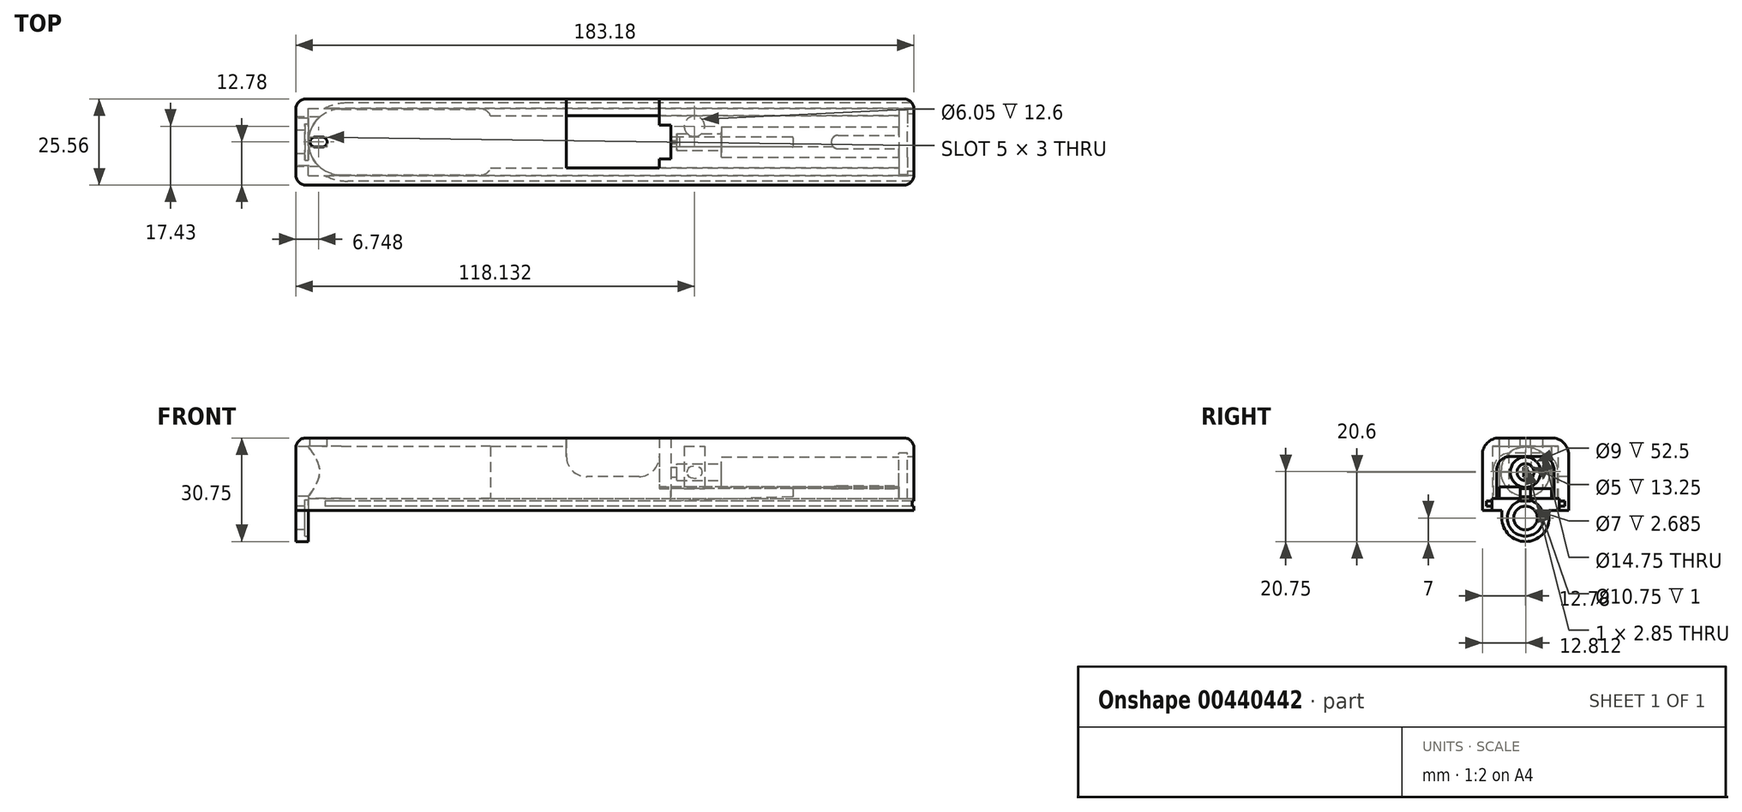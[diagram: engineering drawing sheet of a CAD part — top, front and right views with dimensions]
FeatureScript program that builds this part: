
annotation { "Feature Type Name" : "Feature", "Feature Type Description" : "" }
export const myFeature = defineFeature(function(context is Context, id is Id, definition is map)
    precondition{}
    {
        {
            var Q0;
            Q0=qCreatedBy(makeId("Top.planeOp"),FACE);
            var sketch = newSketch(context, id + "F0", { "sketchPlane" : qUnion([Q0])});
            skLineSegment(sketch, "E0.bottom", {"start": v(91.6, 12.78) * mm, "end": v(-91.6, 12.78) * mm});
            skLineSegment(sketch, "E0.top", {"start": v(91.6, -12.78) * mm, "end": v(-91.6, -12.78) * mm});
            skLineSegment(sketch, "E0.left", {"start": v(91.6, 12.78) * mm, "end": v(91.6, -12.78) * mm});
            skLineSegment(sketch, "E0.right", {"start": v(-91.6, 12.78) * mm, "end": v(-91.6, -12.78) * mm});
            skPoint(sketch, "E0.middle", {"position": v(0, 0) * mm});
            skSolve(sketch);
        }
        {
            var Q0;
            Q0 = qSketchRegion(id + "F0", true);
            extrude(context, id + "F1", {"entities" : qUnion([Q0]), "depth" : 21.5 * mm});
        }
        {
            var Q0;
            Q0=makeQuery(id+"F1.opExtrude","CAP_EDGE",EDGE,{"disambiguationData":[OSD([sQuery(id+"F0.wireOp",EDGE,"E0.top")])],"isStart":false});
            var Q1;
            Q1=makeQuery(id+"F1.opExtrude","CAP_EDGE",EDGE,{"disambiguationData":[OSD([sQuery(id+"F0.wireOp",EDGE,"E0.bottom")])],"isStart":false});
            fillet(context, id + "F2", {"entities" : qUnion([Q0, Q1]), "radius" : 5 * mm, "allowEdgeOverflow" : false});
        }
        {
            var Q0;
            Q0=makeQuery(id+"F1.opExtrude","SWEPT_EDGE",EDGE,{"disambiguationData":[OSD([sQuery(id+"F0.wireOp",EDGE,"E0.top"),sQuery(id+"F0.wireOp",EDGE,"E0.right")])]});
            var Q1;
            Q1=makeQuery(id+"F2.opFillet","BLEND_EDGE",EDGE,{"blendedFrom":[makeQuery(id+"F1.opExtrude","CAP_EDGE",EDGE,{"disambiguationData":[OSD([sQuery(id+"F0.wireOp",EDGE,"E0.top")])],"isStart":false}),makeQuery(id+"F1.opExtrude","SWEPT_FACE",FACE,{"disambiguationData":[OSD([sQuery(id+"F0.wireOp",EDGE,"E0.right")])]})],"blendedInto":[makeQuery(id+"F1.opExtrude","SWEPT_FACE",FACE,{"disambiguationData":[OSD([sQuery(id+"F0.wireOp",EDGE,"E0.right")])]})]});
            var Q2;
            Q2=makeQuery(id+"F1.opExtrude","CAP_EDGE",EDGE,{"disambiguationData":[OSD([sQuery(id+"F0.wireOp",EDGE,"E0.right")])],"isStart":false});
            var Q3;
            Q3=makeQuery(id+"F2.opFillet","BLEND_EDGE",EDGE,{"blendedFrom":[makeQuery(id+"F1.opExtrude","CAP_EDGE",EDGE,{"disambiguationData":[OSD([sQuery(id+"F0.wireOp",EDGE,"E0.bottom")])],"isStart":false}),makeQuery(id+"F1.opExtrude","SWEPT_FACE",FACE,{"disambiguationData":[OSD([sQuery(id+"F0.wireOp",EDGE,"E0.right")])]})],"blendedInto":[makeQuery(id+"F1.opExtrude","SWEPT_FACE",FACE,{"disambiguationData":[OSD([sQuery(id+"F0.wireOp",EDGE,"E0.right")])]})]});
            var Q4;
            Q4=makeQuery(id+"F1.opExtrude","SWEPT_EDGE",EDGE,{"disambiguationData":[OSD([sQuery(id+"F0.wireOp",EDGE,"E0.bottom"),sQuery(id+"F0.wireOp",EDGE,"E0.right")])]});
            var Q5;
            Q5=makeQuery(id+"F1.opExtrude","SWEPT_EDGE",EDGE,{"disambiguationData":[OSD([sQuery(id+"F0.wireOp",EDGE,"E0.top"),sQuery(id+"F0.wireOp",EDGE,"E0.left")])]});
            var Q6;
            Q6=makeQuery(id+"F2.opFillet","BLEND_EDGE",EDGE,{"blendedFrom":[makeQuery(id+"F1.opExtrude","CAP_EDGE",EDGE,{"disambiguationData":[OSD([sQuery(id+"F0.wireOp",EDGE,"E0.top")])],"isStart":false}),makeQuery(id+"F1.opExtrude","SWEPT_FACE",FACE,{"disambiguationData":[OSD([sQuery(id+"F0.wireOp",EDGE,"E0.left")])]})],"blendedInto":[makeQuery(id+"F1.opExtrude","SWEPT_FACE",FACE,{"disambiguationData":[OSD([sQuery(id+"F0.wireOp",EDGE,"E0.left")])]})]});
            var Q7;
            Q7=makeQuery(id+"F1.opExtrude","CAP_EDGE",EDGE,{"disambiguationData":[OSD([sQuery(id+"F0.wireOp",EDGE,"E0.left")])],"isStart":false});
            var Q8;
            Q8=makeQuery(id+"F2.opFillet","BLEND_EDGE",EDGE,{"blendedFrom":[makeQuery(id+"F1.opExtrude","CAP_EDGE",EDGE,{"disambiguationData":[OSD([sQuery(id+"F0.wireOp",EDGE,"E0.bottom")])],"isStart":false}),makeQuery(id+"F1.opExtrude","SWEPT_FACE",FACE,{"disambiguationData":[OSD([sQuery(id+"F0.wireOp",EDGE,"E0.left")])]})],"blendedInto":[makeQuery(id+"F1.opExtrude","SWEPT_FACE",FACE,{"disambiguationData":[OSD([sQuery(id+"F0.wireOp",EDGE,"E0.left")])]})]});
            var Q9;
            Q9=makeQuery(id+"F1.opExtrude","SWEPT_EDGE",EDGE,{"disambiguationData":[OSD([sQuery(id+"F0.wireOp",EDGE,"E0.bottom"),sQuery(id+"F0.wireOp",EDGE,"E0.left")])]});
            fillet(context, id + "F3", {"entities" : qUnion([Q0, Q1, Q2, Q3, Q4, Q5, Q6, Q7, Q8, Q9]), "radius" : 3 * mm, "tangentPropagation" : true, "allowEdgeOverflow" : false});
        }
        {
            var Q0;
            Q0=makeQuery(id+"F1.opExtrude","CAP_FACE",FACE,{"disambiguationData":[OSD([sQuery(id+"F0.wireOp",EDGE,"E0.bottom"),sQuery(id+"F0.wireOp",EDGE,"E0.top"),sQuery(id+"F0.wireOp",EDGE,"E0.left"),sQuery(id+"F0.wireOp",EDGE,"E0.right")])],"isStart":true});
            var sketch = newSketch(context, id + "F4", { "sketchPlane" : qUnion([Q0])});
            skLineSegment(sketch, "E1.bottom", {"start": v(-87.9, 10) * mm, "end": v(91.6, 10) * mm});
            skLineSegment(sketch, "E1.top", {"start": v(-87.9, -10) * mm, "end": v(91.6, -10) * mm});
            skLineSegment(sketch, "E1.left", {"start": v(-87.9, 10) * mm, "end": v(-87.9, -10) * mm});
            skLineSegment(sketch, "E1.right", {"start": v(91.6, 10) * mm, "end": v(91.6, -10) * mm});
            skPoint(sketch, "E1.middle", {"position": v(1.84, 0) * mm});
            skSolve(sketch);
        }
        {
            var Q0;
            Q0 = qSketchRegion(id + "F4", true);
            extrude(context, id + "F5", {"entities" : qUnion([Q0]), "operationType" : NewBodyOperationType.REMOVE, "oppositeDirection" : true, "depth" : 3.5 * mm});
        }
        {
            var Q0;
            Q0=makeQuery(id+"F5.boolean.opBoolean","COPY",FACE,{"derivedFrom":makeQuery(id+"F5.opExtrude","CAP_FACE",FACE,{"disambiguationData":[OSD([sQuery(id+"F4.wireOp",EDGE,"E1.bottom"),sQuery(id+"F4.wireOp",EDGE,"E1.top"),sQuery(id+"F4.wireOp",EDGE,"E1.left"),sQuery(id+"F4.wireOp",EDGE,"E1.right")])],"isStart":false})});
            var sketch = newSketch(context, id + "F6", { "sketchPlane" : qUnion([Q0])});
            skLineSegment(sketch, "E2.bottom", {"start": v(-87.9, -9.75) * mm, "end": v(-33.9, -9.75) * mm});
            skLineSegment(sketch, "E2.top", {"start": v(-87.9, 9.75) * mm, "end": v(-33.9, 9.75) * mm});
            skLineSegment(sketch, "E2.left", {"start": v(-87.9, -9.75) * mm, "end": v(-87.9, 9.75) * mm});
            skLineSegment(sketch, "E2.right", {"start": v(-33.9, -9.75) * mm, "end": v(-33.9, 9.75) * mm});
            skPoint(sketch, "E2.middle", {"position": v(-60.9, 0) * mm});
            skSolve(sketch);
        }
        {
            var Q0;
            Q0 = qSketchRegion(id + "F6", true);
            extrude(context, id + "F7", {"entities" : qUnion([Q0]), "operationType" : NewBodyOperationType.REMOVE, "oppositeDirection" : true, "depth" : 15.5 * mm});
        }
        {
            var Q0;
            Q0=makeQuery(id+"F5.boolean.opBoolean","COPY",FACE,{"derivedFrom":makeQuery(id+"F5.opExtrude","CAP_FACE",FACE,{"disambiguationData":[OSD([sQuery(id+"F4.wireOp",EDGE,"E1.bottom"),sQuery(id+"F4.wireOp",EDGE,"E1.top"),sQuery(id+"F4.wireOp",EDGE,"E1.left"),sQuery(id+"F4.wireOp",EDGE,"E1.right")])],"isStart":false})});
            var sketch = newSketch(context, id + "F8", { "sketchPlane" : qUnion([Q0])});
            skLineSegment(sketch, "E3.bottom", {"start": v(-33.9, -7.75) * mm, "end": v(16.1, -7.75) * mm});
            skLineSegment(sketch, "E3.top", {"start": v(-33.9, 7.75) * mm, "end": v(16.1, 7.75) * mm});
            skLineSegment(sketch, "E3.left", {"start": v(-33.9, -7.75) * mm, "end": v(-33.9, 7.75) * mm});
            skLineSegment(sketch, "E3.right", {"start": v(16.1, -7.75) * mm, "end": v(16.1, 7.75) * mm});
            skPoint(sketch, "E3.middle", {"position": v(-8.9, 0) * mm});
            skSolve(sketch);
        }
        {
            var Q0;
            Q0 = qSketchRegion(id + "F8", true);
            extrude(context, id + "F9", {"entities" : qUnion([Q0]), "operationType" : NewBodyOperationType.REMOVE, "oppositeDirection" : true, "depth" : 15.5 * mm});
        }
        {
            var Q0;
            Q0=makeQuery(id+"F5.boolean.opBoolean","COPY",FACE,{"derivedFrom":makeQuery(id+"F5.opExtrude","CAP_FACE",FACE,{"disambiguationData":[OSD([sQuery(id+"F4.wireOp",EDGE,"E1.bottom"),sQuery(id+"F4.wireOp",EDGE,"E1.top"),sQuery(id+"F4.wireOp",EDGE,"E1.left"),sQuery(id+"F4.wireOp",EDGE,"E1.right")])],"isStart":false})});
            var sketch = newSketch(context, id + "F10", { "sketchPlane" : qUnion([Q0])});
            skLineSegment(sketch, "E4.bottom", {"start": v(19.6, -5) * mm, "end": v(16.1, -5) * mm});
            skLineSegment(sketch, "E4.top", {"start": v(19.6, 5) * mm, "end": v(16.1, 5) * mm});
            skLineSegment(sketch, "E4.left", {"start": v(19.6, -5) * mm, "end": v(19.6, 5) * mm});
            skLineSegment(sketch, "E4.right", {"start": v(16.1, -5) * mm, "end": v(16.1, 5) * mm});
            skSolve(sketch);
        }
        {
            var Q0;
            Q0 = qSketchRegion(id + "F10", true);
            extrude(context, id + "F11", {"entities" : qUnion([Q0]), "operationType" : NewBodyOperationType.REMOVE, "endBound" : BoundingType.THROUGH_ALL, "oppositeDirection" : true, "depth" : 25.4 * mm});
        }
        {
            var Q0;
            Q0=makeQuery(id+"F1.opExtrude","CAP_FACE",FACE,{"disambiguationData":[OSD([sQuery(id+"F0.wireOp",EDGE,"E0.bottom"),sQuery(id+"F0.wireOp",EDGE,"E0.top"),sQuery(id+"F0.wireOp",EDGE,"E0.left"),sQuery(id+"F0.wireOp",EDGE,"E0.right")])],"isStart":false});
            var sketch = newSketch(context, id + "F12", { "sketchPlane" : qUnion([Q0])});
            skLineSegment(sketch, "E5.bottom", {"start": v(-11.4, 7.75) * mm, "end": v(16.1, 7.75) * mm});
            skLineSegment(sketch, "E5.top", {"start": v(-11.4, -7.75) * mm, "end": v(16.1, -7.75) * mm});
            skLineSegment(sketch, "E5.left", {"start": v(-11.4, 7.75) * mm, "end": v(-11.4, -7.75) * mm});
            skLineSegment(sketch, "E5.right", {"start": v(16.1, 7.75) * mm, "end": v(16.1, -7.75) * mm});
            skPoint(sketch, "E5.middle", {"position": v(2.34, 0) * mm});
            skSolve(sketch);
        }
        {
            var Q0;
            {var subQ3=sQuery(id+"F12.wireOp",EDGE,"E5.bottom");Q0=makeQuery(id+"F12.imprint","IMPRINT",FACE,{"disambiguationData":[TD([[makeQuery(id+"F12.imprint","IMPRINT",EDGE,{"derivedFrom":subQ3}),-1.0]])]});}
            extrude(context, id + "F13", {"entities" : qUnion([Q0]), "operationType" : NewBodyOperationType.REMOVE, "oppositeDirection" : true, "depth" : 25.4 * mm});
        }
        {
            var Q0;
            Q0=makeQuery(id+"F13.boolean.opBoolean","MERGE",FACE,{"derivedFrom":[makeQuery(id+"F9.boolean.opBoolean","COPY",FACE,{"derivedFrom":makeQuery(id+"F9.opExtrude","SWEPT_FACE",FACE,{"disambiguationData":[OSD([sQuery(id+"F8.wireOp",EDGE,"E3.top")])]})}),makeQuery(id+"F13.opExtrude","SWEPT_FACE",FACE,{"disambiguationData":[OSD([sQuery(id+"F12.wireOp",EDGE,"E5.top")])]})]});
            var sketch = newSketch(context, id + "F14", { "sketchPlane" : qUnion([Q0])});
            skLineSegment(sketch, "E6.bottom", {"start": v(11.4, 21.5) * mm, "end": v(-16.1, 21.5) * mm});
            skLineSegment(sketch, "E6.top", {"start": v(5.4, 10) * mm, "end": v(-10.1, 10) * mm});
            skLineSegment(sketch, "E6.left", {"start": v(11.4, 21.5) * mm, "end": v(11.4, 16) * mm});
            skLineSegment(sketch, "E6.right", {"start": v(-16.1, 21.5) * mm, "end": v(-16.1, 16) * mm});
            skPoint(sketch, "E6.middle", {"position": v(-2.34, 15.75) * mm});
            skPoint(sketch, "E7.visualSharp", {"position": v(11.4, 10) * mm});
            skArc(sketch, "E7.filletArc", {"start": v(5.4, 10) * mm, "mid": v(9.65, 11.76) * mm, "end": v(11.4, 16) * mm});
            skPoint(sketch, "E8.visualSharp", {"position": v(-16.1, 10) * mm});
            skArc(sketch, "E8.filletArc", {"start": v(-16.1, 16) * mm, "mid": v(-14.34, 11.76) * mm, "end": v(-10.1, 10) * mm});
            skSolve(sketch);
        }
        {
            var Q0;
            Q0 = qSketchRegion(id + "F14", true);
            extrude(context, id + "F15", {"entities" : qUnion([Q0]), "operationType" : NewBodyOperationType.REMOVE, "endBound" : BoundingType.THROUGH_ALL, "depth" : 25.4 * mm});
        }
        {
            var Q0;
            Q0=makeQuery(id+"F7.boolean.opBoolean","COPY",EDGE,{"derivedFrom":makeQuery(id+"F7.opExtrude","SWEPT_EDGE",EDGE,{"disambiguationData":[OSD([sQuery(id+"F4.wireOp",EDGE,"E1.left"),sQuery(id+"F6.wireOp",EDGE,"E2.top"),sQuery(id+"F6.wireOp",EDGE,"E2.left")])]})});
            var Q1;
            Q1=makeQuery(id+"F7.boolean.opBoolean","COPY",EDGE,{"derivedFrom":makeQuery(id+"F7.opExtrude","SWEPT_EDGE",EDGE,{"disambiguationData":[OSD([sQuery(id+"F4.wireOp",EDGE,"E1.left"),sQuery(id+"F6.wireOp",EDGE,"E2.bottom"),sQuery(id+"F6.wireOp",EDGE,"E2.left")])]})});
            fillet(context, id + "F16", {"entities" : qUnion([Q0, Q1]), "radius" : 9.75 * mm, "tangentPropagation" : true, "allowEdgeOverflow" : false});
        }
        {
            var Q0;
            Q0=makeQuery(id+"F7.boolean.opBoolean","COPY",EDGE,{"derivedFrom":makeQuery(id+"F7.opExtrude","SWEPT_EDGE",EDGE,{"disambiguationData":[OSD([sQuery(id+"F6.wireOp",EDGE,"E2.bottom"),sQuery(id+"F6.wireOp",EDGE,"E2.right")])]})});
            var Q1;
            Q1=makeQuery(id+"F7.boolean.opBoolean","COPY",EDGE,{"derivedFrom":makeQuery(id+"F7.opExtrude","SWEPT_EDGE",EDGE,{"disambiguationData":[OSD([sQuery(id+"F6.wireOp",EDGE,"E2.top"),sQuery(id+"F6.wireOp",EDGE,"E2.right")])]})});
            fillet(context, id + "F17", {"entities" : qUnion([Q0, Q1]), "radius" : 3 * mm, "tangentPropagation" : true, "allowEdgeOverflow" : false});
        }
        {
            var Q0;
            Q0=makeQuery(id+"F1.opExtrude","SWEPT_FACE",FACE,{"disambiguationData":[OSD([sQuery(id+"F0.wireOp",EDGE,"E0.right")])]});
            var sketch = newSketch(context, id + "F18", { "sketchPlane" : qUnion([Q0])});
            skCircle(sketch, "E9", {"center": v(-0.03, 11.5) * mm, "radius": 7.38 * mm});
            skPoint(sketch, "E9.centerSnap0", {"position": v(9.78, 9.25) * mm});
            skSolve(sketch);
        }
        {
            var Q0;
            {var subQ0=sQuery(id+"F0.wireOp",EDGE,"E0.right");Q0=makeQuery(id+"F18.imprint","IMPRINT",FACE,{"disambiguationData":[TD([[makeQuery(id+"F18.imprint","IMPRINT",EDGE,{"derivedFrom":makeQuery(id+"F1.opExtrude","CAP_EDGE",EDGE,{"disambiguationData":[OSD([subQ0])],"isStart":true})}),1.0]])]});}
            var sketch = newSketch(context, id + "F19", { "sketchPlane" : qUnion([Q0])});
            skArc(sketch, "E10", {"start": v(-7, -2.25) * mm, "mid": v(0, -9.25) * mm, "end": v(7, -2.25) * mm});
            skLineSegment(sketch, "E11", {"start": v(-7, -2.25) * mm, "end": v(-7, 0) * mm});
            skLineSegment(sketch, "E12", {"start": v(7, -2.25) * mm, "end": v(7, 0) * mm});
            skSolve(sketch);
        }
        {
            var Q0;
            Q0=makeQuery(id+"F19.imprint","IMPRINT",FACE,{"disambiguationData":[TD([[makeQuery(id+"F19.imprint","IMPRINT",EDGE,{"derivedFrom":sQuery(id+"F19.wireOp",EDGE,"E10")}),1.0]])]});
            var Q1;
            {var subQ0=sQuery(id+"F19.wireOp",EDGE,"GewOvBUr-jWPc-clvk-sdnD-IvR5R9FXg0z8");var subQ1=makeQuery(id+"F18.imprint","IMPRINT",EDGE,{"derivedFrom":makeQuery(id+"F1.opExtrude","CAP_EDGE",EDGE,{"disambiguationData":[OSD([sQuery(id+"F0.wireOp",EDGE,"E0.right")])],"isStart":true})});var subQ2=makeQuery(id+"F19.imprint","INTERSECT",VERTEX,{"disambiguationData":[OD(0.0)],"derivedFrom":[subQ1,subQ0]});Q1=makeQuery(id+"F19.imprint","IMPRINT",FACE,{"disambiguationData":[TD([[makeQuery(id+"F19.imprint","IMPRINT",EDGE,{"disambiguationData":[TD([[subQ2,1.0]])],"derivedFrom":subQ0}),1.0]])]});}
            var Q2;
            {var subQ0=sQuery(id+"F19.wireOp",EDGE,"GewOvBUr-jWPc-clvk-sdnD-IvR5R9FXg0z8");var subQ1=makeQuery(id+"F18.imprint","IMPRINT",EDGE,{"derivedFrom":makeQuery(id+"F1.opExtrude","CAP_EDGE",EDGE,{"disambiguationData":[OSD([sQuery(id+"F0.wireOp",EDGE,"E0.right")])],"isStart":true})});var subQ2=makeQuery(id+"F19.imprint","INTERSECT",VERTEX,{"disambiguationData":[OD(0.0)],"derivedFrom":[subQ1,subQ0]});Q2=makeQuery(id+"F19.imprint","IMPRINT",FACE,{"disambiguationData":[TD([[makeQuery(id+"F19.imprint","IMPRINT",EDGE,{"disambiguationData":[TD([[subQ2,-1.0]])],"derivedFrom":subQ0}),1.0]])]});}
            var Q3;
            Q3=makeQuery(id+"F7.boolean.opBoolean","MERGE",FACE,{"derivedFrom":[makeQuery(id+"F5.boolean.opBoolean","COPY",FACE,{"derivedFrom":makeQuery(id+"F5.opExtrude","SWEPT_FACE",FACE,{"disambiguationData":[OSD([sQuery(id+"F4.wireOp",EDGE,"E1.left")])]})}),makeQuery(id+"F7.opExtrude","SWEPT_FACE",FACE,{"disambiguationData":[OSD([sQuery(id+"F6.wireOp",EDGE,"E2.left")])]})]});
            extrude(context, id + "F20", {"entities" : qUnion([Q0, Q1, Q2]), "operationType" : NewBodyOperationType.ADD, "endBound" : BoundingType.UP_TO_SURFACE, "oppositeDirection" : true, "endBoundEntityFace" : qUnion([Q3]), "depth" : 25.4 * mm});
        }
        {
            var Q0;
            {var subQ0=sQuery(id+"F0.wireOp",EDGE,"E0.right");Q0=makeQuery(id+"F20.boolean.opBoolean","MERGE",FACE,{"derivedFrom":[makeQuery(id+"F1.opExtrude","SWEPT_FACE",FACE,{"disambiguationData":[OSD([subQ0])]}),makeQuery(id+"F20.opExtrude","CAP_FACE",FACE,{"disambiguationData":[OSD([subQ0,sQuery(id+"F19.wireOp",EDGE,"E10"),sQuery(id+"F19.wireOp",EDGE,"E11"),sQuery(id+"F19.wireOp",EDGE,"E12")])],"isStart":true})]});}
            var sketch = newSketch(context, id + "F21", { "sketchPlane" : qUnion([Q0])});
            skCircle(sketch, "E13", {"center": v(0, -2.25) * mm, "radius": 3.5 * mm});
            skSolve(sketch);
        }
        {
            var Q0;
            Q0 = qSketchRegion(id + "F21", true);
            extrude(context, id + "F22", {"entities" : qUnion([Q0]), "operationType" : NewBodyOperationType.REMOVE, "endBound" : BoundingType.THROUGH_ALL, "oppositeDirection" : true, "depth" : 25.4 * mm});
        }
        {
            var Q0;
            Q0 = qSketchRegion(id + "F18", true);
            var Q1;
            Q1=makeQuery(id+"F1.opExtrude","SWEPT_BODY",BODY,{"disambiguationData":[OSD([sQuery(id+"F0.wireOp",EDGE,"E0.bottom"),sQuery(id+"F0.wireOp",EDGE,"E0.top"),sQuery(id+"F0.wireOp",EDGE,"E0.left"),sQuery(id+"F0.wireOp",EDGE,"E0.right")])]});
            extrude(context, id + "F23", {"entities" : qUnion([Q0]), "operationType" : NewBodyOperationType.REMOVE, "endBound" : BoundingType.UP_TO_BODY, "oppositeDirection" : true, "endBoundEntityBody" : qUnion([Q1]), "depth" : 25.4 * mm});
        }
        {
            var Q0;
            Q0=makeQuery(id+"F5.boolean.opBoolean","COPY",FACE,{"derivedFrom":makeQuery(id+"F5.opExtrude","CAP_FACE",FACE,{"disambiguationData":[OSD([sQuery(id+"F4.wireOp",EDGE,"E1.bottom"),sQuery(id+"F4.wireOp",EDGE,"E1.top"),sQuery(id+"F4.wireOp",EDGE,"E1.left"),sQuery(id+"F4.wireOp",EDGE,"E1.right")])],"isStart":false})});
            var sketch = newSketch(context, id + "F24", { "sketchPlane" : qUnion([Q0])});
            skLineSegment(sketch, "E14.bottom", {"start": v(91.6, -7.75) * mm, "end": v(-38.4, -7.75) * mm});
            skLineSegment(sketch, "E14.top", {"start": v(91.6, 7.75) * mm, "end": v(-38.4, 7.75) * mm});
            skLineSegment(sketch, "E14.left", {"start": v(91.6, -7.75) * mm, "end": v(91.6, 7.75) * mm});
            skLineSegment(sketch, "E14.right", {"start": v(-38.4, -7.75) * mm, "end": v(-38.4, 7.75) * mm});
            skPoint(sketch, "E14.middle", {"position": v(26.6, 0) * mm});
            skSolve(sketch);
        }
        {
            var Q0;
            Q0 = qSketchRegion(id + "F24", true);
            extrude(context, id + "F25", {"entities" : qUnion([Q0]), "operationType" : NewBodyOperationType.REMOVE, "oppositeDirection" : true, "depth" : 3 * mm});
        }
        {
            var Q0;
            Q0=makeQuery(id+"F25.boolean.opBoolean","COPY",FACE,{"derivedFrom":makeQuery(id+"F25.opExtrude","CAP_FACE",FACE,{"disambiguationData":[OSD([sQuery(id+"F24.wireOp",EDGE,"E14.bottom"),sQuery(id+"F24.wireOp",EDGE,"E14.top"),sQuery(id+"F24.wireOp",EDGE,"E14.left"),sQuery(id+"F24.wireOp",EDGE,"E14.right")])],"isStart":false})});
            var sketch = newSketch(context, id + "F26", { "sketchPlane" : qUnion([Q0])});
            skLineSegment(sketch, "E15.bottom", {"start": v(91.6, 7.75) * mm, "end": v(16.1, 7.75) * mm});
            skLineSegment(sketch, "E15.top", {"start": v(91.6, 1.5) * mm, "end": v(16.1, 1.5) * mm});
            skLineSegment(sketch, "E15.left", {"start": v(91.6, 7.75) * mm, "end": v(91.6, 1.5) * mm});
            skLineSegment(sketch, "E15.right", {"start": v(16.1, 7.75) * mm, "end": v(16.1, 1.5) * mm});
            skSolve(sketch);
        }
        {
            var Q0;
            Q0 = qSketchRegion(id + "F26", true);
            extrude(context, id + "F27", {"entities" : qUnion([Q0]), "operationType" : NewBodyOperationType.REMOVE, "oppositeDirection" : true, "depth" : 0.5 * mm});
        }
        {
            var Q0;
            Q0=makeQuery(id+"F5.boolean.opBoolean","COPY",FACE,{"derivedFrom":makeQuery(id+"F5.opExtrude","SWEPT_FACE",FACE,{"disambiguationData":[OSD([sQuery(id+"F4.wireOp",EDGE,"E1.top")])]})});
            var sketch = newSketch(context, id + "F28", { "sketchPlane" : qUnion([Q0])});
            skLineSegment(sketch, "E16.bottom", {"start": v(91.6, 2.75) * mm, "end": v(-82.9, 2.75) * mm});
            skLineSegment(sketch, "E16.top", {"start": v(91.6, 1.25) * mm, "end": v(-82.9, 1.25) * mm});
            skLineSegment(sketch, "E16.left", {"start": v(91.6, 2.75) * mm, "end": v(91.6, 1.25) * mm});
            skLineSegment(sketch, "E16.right", {"start": v(-82.9, 2.75) * mm, "end": v(-82.9, 1.25) * mm});
            skSolve(sketch);
        }
        {
            var Q0;
            Q0 = qSketchRegion(id + "F28", true);
            extrude(context, id + "F29", {"entities" : qUnion([Q0]), "operationType" : NewBodyOperationType.REMOVE, "oppositeDirection" : true, "depth" : 1.6 * mm});
        }
        {
            var Q0;
            Q0=makeQuery(id+"F29.boolean.opBoolean","COPY",EDGE,{"derivedFrom":makeQuery(id+"F29.opExtrude","CAP_EDGE",EDGE,{"disambiguationData":[OSD([sQuery(id+"F28.wireOp",EDGE,"E16.right")])],"isStart":false})});
            fillet(context, id + "F30", {"entities" : qUnion([Q0]), "radius" : 15 * mm, "tangentPropagation" : true, "allowEdgeOverflow" : false});
        }
        {
            var Q0;
            Q0=makeQuery(id+"F5.boolean.opBoolean","COPY",FACE,{"derivedFrom":makeQuery(id+"F5.opExtrude","SWEPT_FACE",FACE,{"disambiguationData":[OSD([sQuery(id+"F4.wireOp",EDGE,"E1.bottom")])]})});
            var sketch = newSketch(context, id + "F31", { "sketchPlane" : qUnion([Q0])});
            skLineSegment(sketch, "E17.bottom", {"start": v(-91.6, 2.75) * mm, "end": v(82.9, 2.75) * mm});
            skLineSegment(sketch, "E17.top", {"start": v(-91.6, 1.25) * mm, "end": v(82.9, 1.25) * mm});
            skLineSegment(sketch, "E17.left", {"start": v(-91.6, 2.75) * mm, "end": v(-91.6, 1.25) * mm});
            skLineSegment(sketch, "E17.right", {"start": v(82.9, 2.75) * mm, "end": v(82.9, 1.25) * mm});
            skSolve(sketch);
        }
        {
            var Q0;
            Q0 = qSketchRegion(id + "F31", true);
            extrude(context, id + "F32", {"entities" : qUnion([Q0]), "operationType" : NewBodyOperationType.REMOVE, "oppositeDirection" : true, "depth" : 1.6 * mm});
        }
        {
            var Q0;
            Q0=makeQuery(id+"F32.boolean.opBoolean","COPY",EDGE,{"derivedFrom":makeQuery(id+"F32.opExtrude","CAP_EDGE",EDGE,{"disambiguationData":[OSD([sQuery(id+"F31.wireOp",EDGE,"E17.right")])],"isStart":false})});
            fillet(context, id + "F33", {"entities" : qUnion([Q0]), "radius" : 15 * mm, "tangentPropagation" : true, "allowEdgeOverflow" : false});
        }
        {
            var Q0;
            Q0=makeQuery(id+"F1.opExtrude","SWEPT_FACE",FACE,{"disambiguationData":[OSD([sQuery(id+"F0.wireOp",EDGE,"E0.left")])]});
            var sketch = newSketch(context, id + "F34", { "sketchPlane" : qUnion([Q0])});
            skLineSegment(sketch, "E18.bottom", {"start": v(-8.53, 0) * mm, "end": v(8.47, 0) * mm});
            skLineSegment(sketch, "E18.top", {"start": v(-4.53, 16) * mm, "end": v(4.47, 16) * mm});
            skLineSegment(sketch, "E18.left", {"start": v(-8.53, 0) * mm, "end": v(-8.53, 12) * mm});
            skLineSegment(sketch, "E18.right", {"start": v(8.47, 0) * mm, "end": v(8.47, 12) * mm});
            skPoint(sketch, "E18.middle", {"position": v(-0.03, 8) * mm});
            skPoint(sketch, "E19.visualSharp", {"position": v(8.47, 16) * mm});
            skArc(sketch, "E19.filletArc", {"start": v(8.47, 12) * mm, "mid": v(7.3, 14.83) * mm, "end": v(4.47, 16) * mm});
            skPoint(sketch, "E20.visualSharp", {"position": v(-8.53, 16) * mm});
            skArc(sketch, "E20.filletArc", {"start": v(-4.53, 16) * mm, "mid": v(-7.36, 14.83) * mm, "end": v(-8.53, 12) * mm});
            skSolve(sketch);
        }
        {
            var Q0;
            Q0 = qSketchRegion(id + "F34", true);
            extrude(context, id + "F35", {"entities" : qUnion([Q0]), "operationType" : NewBodyOperationType.REMOVE, "oppositeDirection" : true, "depth" : 4.5 * mm});
        }
        {
            var Q0;
            Q0=makeQuery(id+"F35.boolean.opBoolean","COPY",FACE,{"derivedFrom":makeQuery(id+"F35.opExtrude","CAP_FACE",FACE,{"disambiguationData":[OSD([sQuery(id+"F34.wireOp",EDGE,"E18.bottom"),sQuery(id+"F34.wireOp",EDGE,"E18.top"),sQuery(id+"F34.wireOp",EDGE,"E18.left"),sQuery(id+"F34.wireOp",EDGE,"E18.right"),sQuery(id+"F34.wireOp",EDGE,"E19.filletArc"),sQuery(id+"F34.wireOp",EDGE,"E20.filletArc")])],"isStart":false})});
            var sketch = newSketch(context, id + "F36", { "sketchPlane" : qUnion([Q0])});
            skLineSegment(sketch, "E21.0", {"start": v(8.47, 3.5) * mm, "end": v(8.47, 12) * mm});
            skArc(sketch, "E22.0", {"start": v(8.47, 12) * mm, "mid": v(7.3, 14.83) * mm, "end": v(4.47, 16) * mm});
            skLineSegment(sketch, "E23.0", {"start": v(-4.53, 16) * mm, "end": v(4.47, 16) * mm});
            skArc(sketch, "E24.0", {"start": v(-4.53, 16) * mm, "mid": v(-7.36, 14.83) * mm, "end": v(-8.53, 12) * mm});
            skLineSegment(sketch, "E25.0", {"start": v(-8.53, 3.5) * mm, "end": v(-8.53, 12) * mm});
            skLineSegment(sketch, "E26.0", {"start": v(6.75, 2.5) * mm, "end": v(9.47, 2.5) * mm});
            skLineSegment(sketch, "E26.1", {"start": v(6.75, 5.5) * mm, "end": v(6.75, 2.5) * mm});
            skLineSegment(sketch, "E26.2", {"start": v(9.47, 2.5) * mm, "end": v(9.47, 12) * mm});
            skLineSegment(sketch, "E26.3", {"start": v(-6.75, 5.5) * mm, "end": v(6.75, 5.5) * mm});
            skLineSegment(sketch, "E26.4", {"start": v(-6.75, 2.5) * mm, "end": v(-6.75, 5.5) * mm});
            skLineSegment(sketch, "E26.5", {"start": v(-9.53, 2.5) * mm, "end": v(-6.75, 2.5) * mm});
            skArc(sketch, "E26.6", {"start": v(9.47, 12) * mm, "mid": v(8, 15.54) * mm, "end": v(4.47, 17) * mm});
            skLineSegment(sketch, "E26.7", {"start": v(4.47, 17) * mm, "end": v(-4.53, 17) * mm});
            skArc(sketch, "E26.8", {"start": v(-4.53, 17) * mm, "mid": v(-8.07, 15.54) * mm, "end": v(-9.53, 12) * mm});
            skLineSegment(sketch, "E26.9", {"start": v(-9.53, 12) * mm, "end": v(-9.53, 2.5) * mm});
            skSolve(sketch);
        }
        {
            var Q0;
            {var subQ13=sQuery(id+"F36.wireOp",EDGE,"E21.0");Q0=makeQuery(id+"F36.imprint","IMPRINT",FACE,{"disambiguationData":[TD([[makeQuery(id+"F36.imprint","IMPRINT",EDGE,{"derivedFrom":subQ13}),-1.0]])]});}
            extrude(context, id + "F37", {"entities" : qUnion([Q0]), "operationType" : NewBodyOperationType.REMOVE, "depth" : 2.5 * mm});
        }
        {
            var Q0;
            {var subQ0=sQuery(id+"F6.wireOp",EDGE,"E2.left");var subQ1=sQuery(id+"F4.wireOp",EDGE,"E1.left");Q0=makeQuery(id+"F20.boolean.opBoolean","MERGE",FACE,{"derivedFrom":[makeQuery(id+"F7.boolean.opBoolean","MERGE",FACE,{"derivedFrom":[makeQuery(id+"F5.boolean.opBoolean","COPY",FACE,{"derivedFrom":makeQuery(id+"F5.opExtrude","SWEPT_FACE",FACE,{"disambiguationData":[OSD([subQ1])]})}),makeQuery(id+"F7.opExtrude","SWEPT_FACE",FACE,{"disambiguationData":[OSD([subQ0])]})]}),makeQuery(id+"F20.opExtrude","CAP_FACE",FACE,{"disambiguationData":[OSD([subQ1,subQ0])],"isStart":false})]});}
            var sketch = newSketch(context, id + "F38", { "sketchPlane" : qUnion([Q0])});
            skCircle(sketch, "E27", {"center": v(0, -2.25) * mm, "radius": 5.38 * mm});
            skSolve(sketch);
        }
        {
            var Q0;
            Q0 = qSketchRegion(id + "F38", true);
            extrude(context, id + "F39", {"entities" : qUnion([Q0]), "operationType" : NewBodyOperationType.REMOVE, "oppositeDirection" : true, "depth" : 1 * mm});
        }
        {
            var Q0;
            {var subQ0=sQuery(id+"F34.wireOp",EDGE,"E20.filletArc");var subQ1=sQuery(id+"F34.wireOp",EDGE,"E19.filletArc");var subQ2=sQuery(id+"F34.wireOp",EDGE,"E18.right");var subQ3=sQuery(id+"F34.wireOp",EDGE,"E18.left");var subQ4=sQuery(id+"F34.wireOp",EDGE,"E18.top");var subQ5=sQuery(id+"F34.wireOp",EDGE,"E18.bottom");Q0=makeQuery(id+"F37.boolean.opBoolean","MERGE",FACE,{"derivedFrom":[makeQuery(id+"F35.boolean.opBoolean","COPY",FACE,{"derivedFrom":makeQuery(id+"F35.opExtrude","CAP_FACE",FACE,{"disambiguationData":[OSD([subQ5,subQ4,subQ3,subQ2,subQ1,subQ0])],"isStart":false})}),makeQuery(id+"F37.opExtrude","CAP_FACE",FACE,{"disambiguationData":[OSD([sQuery(id+"F4.wireOp",EDGE,"E1.bottom"),sQuery(id+"F4.wireOp",EDGE,"E1.top"),sQuery(id+"F4.wireOp",EDGE,"E1.left"),sQuery(id+"F4.wireOp",EDGE,"E1.right"),sQuery(id+"F8.wireOp",EDGE,"E3.bottom"),sQuery(id+"F8.wireOp",EDGE,"E3.top"),sQuery(id+"F12.wireOp",EDGE,"E5.bottom"),sQuery(id+"F12.wireOp",EDGE,"E5.top"),sQuery(id+"F24.wireOp",EDGE,"E14.bottom"),sQuery(id+"F24.wireOp",EDGE,"E14.top"),sQuery(id+"F24.wireOp",EDGE,"E14.left"),sQuery(id+"F24.wireOp",EDGE,"E14.right"),sQuery(id+"F26.wireOp",EDGE,"E15.bottom"),sQuery(id+"F26.wireOp",EDGE,"E15.top"),sQuery(id+"F26.wireOp",EDGE,"E15.left"),sQuery(id+"F26.wireOp",EDGE,"E15.right"),subQ5,subQ4,subQ3,subQ2,subQ1,subQ0,sQuery(id+"F36.wireOp",EDGE,"E21.0"),sQuery(id+"F36.wireOp",EDGE,"E22.0"),sQuery(id+"F36.wireOp",EDGE,"E23.0"),sQuery(id+"F36.wireOp",EDGE,"E24.0"),sQuery(id+"F36.wireOp",EDGE,"E25.0"),sQuery(id+"F36.wireOp",EDGE,"E26.0"),sQuery(id+"F36.wireOp",EDGE,"E26.1"),sQuery(id+"F36.wireOp",EDGE,"E26.2"),sQuery(id+"F36.wireOp",EDGE,"E26.3"),sQuery(id+"F36.wireOp",EDGE,"E26.4"),sQuery(id+"F36.wireOp",EDGE,"E26.5"),sQuery(id+"F36.wireOp",EDGE,"E26.6"),sQuery(id+"F36.wireOp",EDGE,"E26.7"),sQuery(id+"F36.wireOp",EDGE,"E26.8"),sQuery(id+"F36.wireOp",EDGE,"E26.9")])],"isStart":true})]});}
            var sketch = newSketch(context, id + "F40", { "sketchPlane" : qUnion([Q0])});
            skCircle(sketch, "E28", {"center": v(0, 11.35) * mm, "radius": 4.5 * mm});
            skCircle(sketch, "E29", {"center": v(0, 11.35) * mm, "radius": 2.5 * mm});
            skLineSegment(sketch, "E30.bottom", {"start": v(0.5, 12.78) * mm, "end": v(-0.5, 12.78) * mm});
            skLineSegment(sketch, "E30.top", {"start": v(0.5, 9.93) * mm, "end": v(-0.5, 9.93) * mm});
            skLineSegment(sketch, "E30.left", {"start": v(0.5, 12.78) * mm, "end": v(0.5, 9.93) * mm});
            skLineSegment(sketch, "E30.right", {"start": v(-0.5, 12.78) * mm, "end": v(-0.5, 9.93) * mm});
            skSolve(sketch);
        }
        {
            var Q0;
            Q0=makeQuery(id+"F40.imprint","IMPRINT",FACE,{"disambiguationData":[TD([[makeQuery(id+"F40.imprint","IMPRINT",EDGE,{"derivedFrom":sQuery(id+"F40.wireOp",EDGE,"E30.bottom")}),1.0]])]});
            extrude(context, id + "F41", {"entities" : qUnion([Q0]), "operationType" : NewBodyOperationType.REMOVE, "endBound" : BoundingType.THROUGH_ALL, "oppositeDirection" : true, "depth" : 25.4 * mm});
        }
        {
            var Q0;
            Q0=makeQuery(id+"F40.imprint","IMPRINT",FACE,{"disambiguationData":[TD([[makeQuery(id+"F40.imprint","IMPRINT",EDGE,{"derivedFrom":sQuery(id+"F40.wireOp",EDGE,"E29")}),1.0]])]});
            var Q1;
            Q1=makeQuery(id+"F40.imprint","IMPRINT",FACE,{"disambiguationData":[TD([[makeQuery(id+"F40.imprint","IMPRINT",EDGE,{"derivedFrom":sQuery(id+"F40.wireOp",EDGE,"E30.bottom")}),1.0]])]});
            extrude(context, id + "F42", {"entities" : qUnion([Q0, Q1]), "operationType" : NewBodyOperationType.REMOVE, "oppositeDirection" : true, "depth" : 65.75 * mm});
        }
        {
            var Q0;
            Q0=makeQuery(id+"F40.imprint","IMPRINT",FACE,{"disambiguationData":[TD([[makeQuery(id+"F40.imprint","IMPRINT",EDGE,{"derivedFrom":sQuery(id+"F40.wireOp",EDGE,"E29")}),1.0]])]});
            var Q1;
            Q1=makeQuery(id+"F40.imprint","IMPRINT",FACE,{"disambiguationData":[TD([[makeQuery(id+"F40.imprint","IMPRINT",EDGE,{"derivedFrom":sQuery(id+"F40.wireOp",EDGE,"E28")}),1.0]])]});
            extrude(context, id + "F43", {"entities" : qUnion([Q0, Q1]), "operationType" : NewBodyOperationType.REMOVE, "oppositeDirection" : true, "depth" : 52.5 * mm});
        }
        {
            var Q0;
            Q0=makeQuery(id+"F27.boolean.opBoolean","COPY",FACE,{"derivedFrom":makeQuery(id+"F27.opExtrude","CAP_FACE",FACE,{"disambiguationData":[OSD([sQuery(id+"F26.wireOp",EDGE,"E15.bottom"),sQuery(id+"F26.wireOp",EDGE,"E15.top"),sQuery(id+"F26.wireOp",EDGE,"E15.left"),sQuery(id+"F26.wireOp",EDGE,"E15.right")])],"isStart":false})});
            var sketch = newSketch(context, id + "F44", { "sketchPlane" : qUnion([Q0])});
            skLineSegment(sketch, "E31.bottom", {"start": v(87.1, 2) * mm, "end": v(69.1, 2) * mm});
            skLineSegment(sketch, "E31.top", {"start": v(87.1, -2) * mm, "end": v(69.1, -2) * mm});
            skLineSegment(sketch, "E31.left", {"start": v(87.1, 2) * mm, "end": v(87.1, -2) * mm});
            skArc(sketch, "E32", {"start": v(69.1, 2) * mm, "mid": v(67.1, 0) * mm, "end": v(69.1, -2) * mm});
            skSolve(sketch);
        }
        {
            var Q0;
            Q0 = qSketchRegion(id + "F44", true);
            extrude(context, id + "F45", {"entities" : qUnion([Q0]), "operationType" : NewBodyOperationType.REMOVE, "endBound" : BoundingType.SYMMETRIC, "depth" : 4.5 * mm});
        }
        {
            var Q0;
            Q0=makeQuery(id+"F25.boolean.opBoolean","COPY",FACE,{"derivedFrom":makeQuery(id+"F25.opExtrude","CAP_FACE",FACE,{"disambiguationData":[OSD([sQuery(id+"F24.wireOp",EDGE,"E14.bottom"),sQuery(id+"F24.wireOp",EDGE,"E14.top"),sQuery(id+"F24.wireOp",EDGE,"E14.left"),sQuery(id+"F24.wireOp",EDGE,"E14.right")])],"isStart":false})});
            var sketch = newSketch(context, id + "F46", { "sketchPlane" : qUnion([Q0])});
            skCircle(sketch, "E33", {"center": v(26.54, -4.65) * mm, "radius": 3.03 * mm});
            skSolve(sketch);
        }
        {
            var Q0;
            Q0 = qSketchRegion(id + "F46", true);
            extrude(context, id + "F47", {"entities" : qUnion([Q0]), "operationType" : NewBodyOperationType.REMOVE, "oppositeDirection" : true, "depth" : 12.6 * mm});
        }
        {
            var Q0;
            Q0=makeQuery(id+"F27.boolean.opBoolean","COPY",FACE,{"derivedFrom":makeQuery(id+"F27.opExtrude","SWEPT_FACE",FACE,{"disambiguationData":[OSD([sQuery(id+"F26.wireOp",EDGE,"E15.top")])]})});
            var sketch = newSketch(context, id + "F48", { "sketchPlane" : qUnion([Q0])});
            skLineSegment(sketch, "E34", {"start": v(55.74, 6.5) * mm, "end": v(55.74, 4.1) * mm});
            skLineSegment(sketch, "E35", {"start": v(19.6, 2.85) * mm, "end": v(19.6, 6.5) * mm});
            skLineSegment(sketch, "E36", {"start": v(19.6, 6.5) * mm, "end": v(55.74, 6.5) * mm});
            skLineSegment(sketch, "E37", {"start": v(55.74, 4.1) * mm, "end": v(22.1, 2.85) * mm});
            skLineSegment(sketch, "E38", {"start": v(22.1, 2.85) * mm, "end": v(19.6, 2.85) * mm});
            skSolve(sketch);
        }
        {
            var Q0;
            Q0 = qSketchRegion(id + "F48", true);
            extrude(context, id + "F49", {"entities" : qUnion([Q0]), "operationType" : NewBodyOperationType.ADD, "oppositeDirection" : true, "depth" : 3 * mm});
        }
        {
            var Q0;
            Q0=makeQuery(id+"F49.opExtrude","CAP_EDGE",EDGE,{"disambiguationData":[OSD([sQuery(id+"F48.wireOp",EDGE,"E34")])],"isStart":true});
            var Q1;
            Q1=makeQuery(id+"F49.opExtrude","CAP_EDGE",EDGE,{"disambiguationData":[OSD([sQuery(id+"F48.wireOp",EDGE,"E34")])],"isStart":false});
            fillet(context, id + "F50", {"entities" : qUnion([Q0, Q1]), "radius" : 0.25 * mm, "tangentPropagation" : true, "allowEdgeOverflow" : false});
        }
        {
            var Q0;
            Q0=makeQuery(id+"F1.opExtrude","CAP_FACE",FACE,{"disambiguationData":[OSD([sQuery(id+"F0.wireOp",EDGE,"E0.bottom"),sQuery(id+"F0.wireOp",EDGE,"E0.top"),sQuery(id+"F0.wireOp",EDGE,"E0.left"),sQuery(id+"F0.wireOp",EDGE,"E0.right")])],"isStart":false});
            var sketch = newSketch(context, id + "F51", { "sketchPlane" : qUnion([Q0])});
            skLineSegment(sketch, "E39.bottom", {"start": v(-85.84, -1.5) * mm, "end": v(-83.84, -1.5) * mm});
            skLineSegment(sketch, "E39.top", {"start": v(-85.84, 1.5) * mm, "end": v(-83.84, 1.5) * mm});
            skPoint(sketch, "E39.middle", {"position": v(-84.84, 0) * mm});
            skArc(sketch, "E40", {"start": v(-83.84, -1.5) * mm, "mid": v(-82.34, 0) * mm, "end": v(-83.84, 1.5) * mm});
            skArc(sketch, "E41", {"start": v(-85.84, 1.5) * mm, "mid": v(-87.34, 0) * mm, "end": v(-85.84, -1.5) * mm});
            skSolve(sketch);
        }
        {
            var Q0;
            Q0 = qSketchRegion(id + "F51", true);
            extrude(context, id + "F52", {"entities" : qUnion([Q0]), "operationType" : NewBodyOperationType.REMOVE, "endBound" : BoundingType.THROUGH_ALL, "oppositeDirection" : true, "depth" : 25.4 * mm});
        }
        {
            var Q0;
            {var subQ0=sQuery(id+"F0.wireOp",EDGE,"E0.right");var subQ1=sQuery(id+"F0.wireOp",EDGE,"E0.bottom");var subQ4=sQuery(id+"F0.wireOp",EDGE,"E0.left");Q0=makeQuery(id+"F20.boolean.opBoolean","SPLIT",FACE,{"disambiguationData":[TD([makeQuery(id+"F1.opExtrude","SWEPT_FACE",FACE,{"disambiguationData":[OSD([subQ1])]})])],"derivedFrom":makeQuery(id+"F1.opExtrude","CAP_FACE",FACE,{"disambiguationData":[OSD([subQ1,sQuery(id+"F0.wireOp",EDGE,"E0.top"),subQ4,subQ0])],"isStart":true})});}
            cPlane(context, id + "F53", {"entities" : qUnion([Q0]), "cplaneType" : CPlaneType.OFFSET, "offset" : 12.72 * mm, "oppositeDirection" : true, "width" : 152.4 * mm, "height" : 152.4 * mm});
        }
    });
